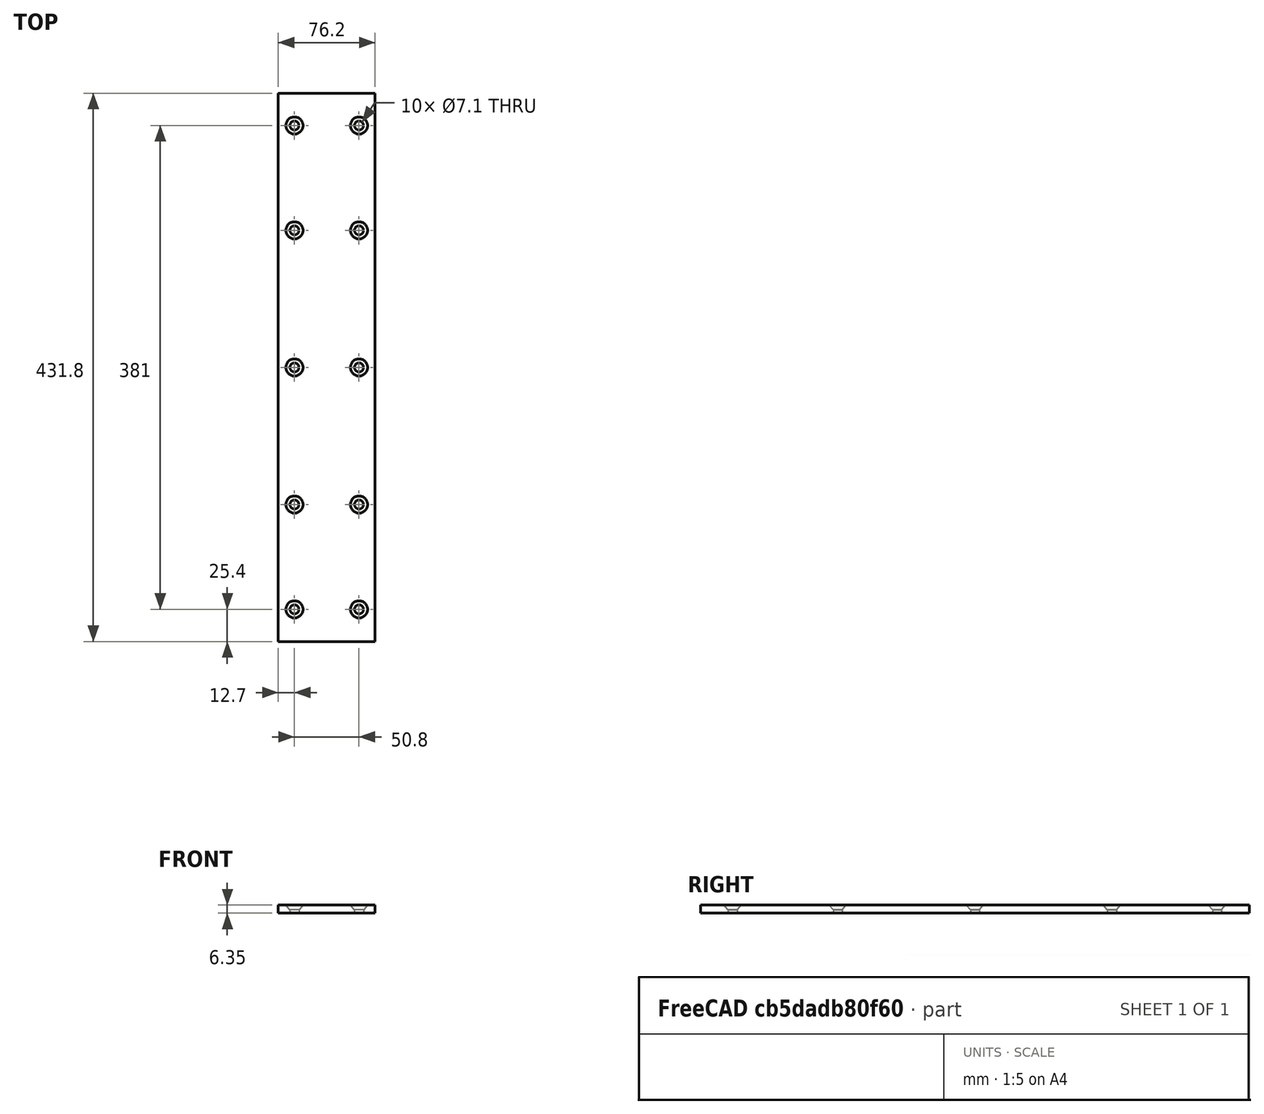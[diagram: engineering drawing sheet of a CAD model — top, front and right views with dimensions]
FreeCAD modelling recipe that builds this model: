
FCSTD DOCUMENT  (FreeCAD 0.20R29603 (Git))
Label: zero_clearance_insert
License: All rights reserved
LicenseURL: http://en.wikipedia.org/wiki/All_rights_reserved
objects: TechDraw::DrawViewDimension×8, TechDraw::DrawProjGroupItem×3, Sketcher::SketchObject×2, PartDesign::Pad×1, PartDesign::Hole×1, PartDesign::Body×1, TechDraw::DrawSVGTemplate×1, TechDraw::DrawProjGroup×1, TechDraw::DrawPage×1
note: 7 computed .brp shape members not serialized (recipe doc carries the construction recipe); baked Part::Feature solids carry a one-line shape summary decoded from their .brp

FEATURE [Sketcher::SketchObject] Sketch
  FullyConstrained = true
  MapMode = 5
  Support = -> [XY_Plane]
  sketch-geometry (5):
    g0: LineSegment StartX=-38.1 StartY=-215.9 StartZ=0 EndX=-38.1 EndY=215.9 EndZ=0
    g1: LineSegment StartX=-38.1 StartY=215.9 StartZ=0 EndX=38.1 EndY=215.9 EndZ=0
    g2: LineSegment StartX=38.1 StartY=215.9 StartZ=0 EndX=38.1 EndY=-215.9 EndZ=0
    g3: LineSegment StartX=38.1 StartY=-215.9 StartZ=0 EndX=-38.1 EndY=-215.9 EndZ=0
    g4: GeomPoint X=0 Y=0 Z=0
  constraints (12):
    c: Coincident(g0,g1)
    c: Coincident(g1,g2)
    c: Coincident(g2,g3)
    c: Coincident(g3,g0)
    c: Horizontal(g1)
    c: Horizontal(g3)
    c: Vertical(g0)
    c: Vertical(g2)
    c: Symmetric(g1,g0,g4)
    c: DistanceX(g1,g1) = 76.2
    c: DistanceY(g2,g2) = 431.8
    c: Coincident(g4,g-1)
FEATURE [PartDesign::Pad] Pad
  Direction = (0,0,1)
  Length = 6.35
  Length2 = 10
  Profile = -> Sketch
  ReferenceAxis = -> Sketch [N_Axis]
  Type = 0
FEATURE [Sketcher::SketchObject] Sketch001
  ExternalGeometry = -> [Pad]
  FullyConstrained = true
  MapMode = 5
  Placement = pos=(0,0,6.35) rot=(0,0,1;0rad)
  Support = -> [Pad]
  sketch-geometry (14):
    g0: LineSegment StartX=-25.4 StartY=215.9 StartZ=0 EndX=-25.4 EndY=-215.9 EndZ=0
    g1: LineSegment StartX=25.4 StartY=-215.9 StartZ=0 EndX=25.4 EndY=215.9 EndZ=0
    g2: Circle CenterX=-25.4 CenterY=190.5 CenterZ=0 NormalX=0 NormalY=0 NormalZ=1 AngleXU=0 Radius=3.175
    g3: Circle CenterX=-25.4 CenterY=0 CenterZ=0 NormalX=0 NormalY=0 NormalZ=1 AngleXU=0 Radius=3.175
    g4: Circle CenterX=-25.4 CenterY=107.95 CenterZ=0 NormalX=0 NormalY=0 NormalZ=1 AngleXU=0 Radius=3.175
    g5: LineSegment StartX=-25.4 StartY=215.9 StartZ=0 EndX=-25.4 EndY=107.95 EndZ=0
    g6: LineSegment StartX=-25.4 StartY=107.95 StartZ=0 EndX=-25.4 EndY=0 EndZ=0
    g7: Circle CenterX=-25.4 CenterY=-190.5 CenterZ=0 NormalX=0 NormalY=0 NormalZ=1 AngleXU=0 Radius=3.175
    g8: Circle CenterX=-25.4 CenterY=-107.95 CenterZ=0 NormalX=0 NormalY=0 NormalZ=1 AngleXU=0 Radius=3.175
    g9: Circle CenterX=25.4 CenterY=-190.5 CenterZ=0 NormalX=0 NormalY=0 NormalZ=1 AngleXU=0 Radius=3.175
    g10: Circle CenterX=25.4 CenterY=-107.95 CenterZ=0 NormalX=0 NormalY=0 NormalZ=1 AngleXU=0 Radius=3.175
    g11: Circle CenterX=25.4 CenterY=0 CenterZ=0 NormalX=0 NormalY=0 NormalZ=1 AngleXU=0 Radius=3.175
    g12: Circle CenterX=25.4 CenterY=107.95 CenterZ=0 NormalX=0 NormalY=0 NormalZ=1 AngleXU=0 Radius=3.175
    g13: Circle CenterX=25.4 CenterY=190.5 CenterZ=0 NormalX=0 NormalY=0 NormalZ=1 AngleXU=0 Radius=3.175
  constraints (43):
    c: Vertical(g0)
    c: Vertical(g1)
    c: PointOnObject(g1,g-3)
    c: PointOnObject(g0,g-3)
    c: PointOnObject(g0,g-6)
    c: PointOnObject(g1,g-6)
    c: Distance(g0,g-6) = 12.7
    c: Distance(g1,g-6) = 12.7
    c: Diameter(g2) = 6.35
    c: PointOnObject(g2,g0)
    c: Distance(g2,g-3) = 25.4
    c: PointOnObject(g3,g-1)
    c: PointOnObject(g3,g0)
    c: Equal(g2,g3)
    c: Equal(g3,g4)
    c: PointOnObject(g4,g0)
    c: Coincident(g5,g4)
    c: PointOnObject(g5,g-3)
    c: Vertical(g5)
    c: Coincident(g6,g3)
    c: Coincident(g6,g4)
    c: Equal(g5,g6)
    c: Distance(g7,g-6) = 25.4
    c: PointOnObject(g7,g0)
    c: Distance(g8,g-6) = 107.95
    c: PointOnObject(g8,g0)
    c: Equal(g8,g7)
    c: Equal(g7,g2)
    c: Diameter(g13) = 6.35
    c: Equal(g13,g11)
    c: Equal(g11,g12)
    c: Equal(g10,g9)
    c: Equal(g9,g13)
    c: Distance(g9,g-6) = 25.4
    c: PointOnObject(g9,g1)
    c: PointOnObject(g10,g1)
    c: PointOnObject(g11,g1)
    c: PointOnObject(g11,g-1)
    c: PointOnObject(g12,g1)
    c: Distance(g13,g-3) = 25.4
    c: PointOnObject(g13,g1)
    c: Distance(g12,g-3) = 107.95
    c: Distance(g10,g-6) = 107.95
FEATURE [PartDesign::Hole] Hole
  BaseFeature = -> Pad
  CustomThreadClearance = 0
  Depth = 885.806
  DepthType = 1
  Diameter = 7.1
  DrillForDepth = false
  DrillPoint = 1
  DrillPointAngle = 118
  HoleCutCountersinkAngle = 81
  HoleCutCustomValues = false
  HoleCutDepth = 0
  HoleCutDiameter = 13.4938
  HoleCutType = 2
  ModelThread = false
  Profile = -> Sketch001
  Tapered = false
  TaperedAngle = 90
  ThreadClass = 0
  ThreadDepth = 885.806
  ThreadDepthType = 0
  ThreadDirection = 0
  ThreadFit = 0
  ThreadSize = 9
  ThreadType = 3
  Threaded = false
  UseCustomThreadClearance = false
FEATURE [PartDesign::Body] Body
  Group = -> [Sketch,Pad,Sketch001,Hole]
  Origin = -> Origin
  Tip = -> Hole
FEATURE [TechDraw::DrawSVGTemplate] Template
  Height = 297
  Orientation = 1
  Width = 420
FEATURE [TechDraw::DrawProjGroupItem] ProjItem  label="Front"
  CoarseView = false
  Direction = (0,0,1)
  Focus = 100
  HardHidden = false
  IsoCount = 0
  IsoHidden = false
  IsoVisible = false
  LockPosition = true
  Perspective = false
  Rotation = 0
  RotationVector = (1,0,0)
  Scale = 0.5
  ScaleType = 2
  SeamHidden = false
  SeamVisible = true
  SmoothHidden = false
  SmoothVisible = true
  Source = -> [Body]
  Type = 0
  X = 0
  XDirection = (1e-16,-1,0)
  Y = 0
FEATURE [TechDraw::DrawProjGroupItem] ProjItem001  label="Left"
  CoarseView = false
  Direction = (-1e-16,1,1e-16)
  Focus = 100
  HardHidden = false
  IsoCount = 0
  IsoHidden = false
  IsoVisible = false
  LockPosition = false
  Perspective = false
  Rotation = 0
  RotationVector = (1,0,0)
  Scale = 0.5
  ScaleType = 2
  SeamHidden = false
  SeamVisible = true
  SmoothHidden = false
  SmoothVisible = true
  Source = -> [Body]
  Type = 1
  X = 230.981
  XDirection = (0,-1e-16,1)
  Y = 0
FEATURE [TechDraw::DrawProjGroupItem] ProjItem002  label="FrontTopRight"
  CoarseView = false
  Direction = (0.57735,-0.57735,0.57735)
  Focus = 100
  HardHidden = false
  IsoCount = 0
  IsoHidden = false
  IsoVisible = false
  LockPosition = false
  Perspective = false
  Rotation = 0
  RotationVector = (1,0,0)
  Scale = 0.5
  ScaleType = 2
  SeamHidden = false
  SeamVisible = true
  SmoothHidden = false
  SmoothVisible = true
  Source = -> [Body]
  Type = 7
  X = 147.001
  XDirection = (0,-0.707107,-0.707107)
  Y = 86.9946
FEATURE [TechDraw::DrawProjGroup] ProjGroup
  Anchor = -> ProjItem
  AutoDistribute = true
  LockPosition = false
  ProjectionType = 0
  Rotation = 0
  Scale = 0.5
  ScaleType = 0
  Source = -> [Body]
  Views = -> [ProjItem,ProjItem001,ProjItem002]
  X = 169.962
  Y = 139.782
  spacingX = 15.0812
  spacingY = 15.0812
FEATURE [TechDraw::DrawViewDimension] Dimension
  AngleOverride = false
  Arbitrary = false
  ArbitraryTolerances = false
  EqualTolerance = true
  ExtensionAngle = 0
  FormatSpec = ⌀%.2w 10x
  FormatSpecOverTolerance = %+.2w
  FormatSpecUnderTolerance = %+.2w
  Inverted = false
  LineAngle = 0
  LockPosition = false
  MeasureType = 1
  OverTolerance = 0
  References2D = -> [ProjItem]
  Rotation = 0
  Scale = 0.5
  ScaleType = 0
  TheoreticalExact = false
  Type = 5
  UnderTolerance = 0
  X = 75.0786
  Y = 40.8996
FEATURE [TechDraw::DrawViewDimension] Dimension001
  AngleOverride = false
  Arbitrary = false
  ArbitraryTolerances = false
  EqualTolerance = true
  ExtensionAngle = 0
  FormatSpec = %.2w
  FormatSpecOverTolerance = %+.2w
  FormatSpecUnderTolerance = %+.2w
  Inverted = false
  LineAngle = 0
  LockPosition = false
  MeasureType = 1
  OverTolerance = 0
  References2D = -> [ProjItem]
  Rotation = 0
  Scale = 0.5
  ScaleType = 0
  TheoreticalExact = false
  Type = 1
  UnderTolerance = 0
  X = -81.4561
  Y = -33.3394
FEATURE [TechDraw::DrawViewDimension] Dimension002
  AngleOverride = false
  Arbitrary = false
  ArbitraryTolerances = false
  EqualTolerance = true
  ExtensionAngle = 0
  FormatSpec = %.2w
  FormatSpecOverTolerance = %+.2w
  FormatSpecUnderTolerance = %+.2w
  Inverted = false
  LineAngle = 0
  LockPosition = false
  MeasureType = 1
  OverTolerance = 0
  References2D = -> [ProjItem]
  Rotation = 0
  Scale = 0.5
  ScaleType = 0
  TheoreticalExact = false
  Type = 0
  UnderTolerance = 0
  X = -73.7758
  Y = -39.1239
FEATURE [TechDraw::DrawViewDimension] Dimension003
  AngleOverride = false
  Arbitrary = false
  ArbitraryTolerances = false
  EqualTolerance = true
  ExtensionAngle = 0
  FormatSpec = %.2w
  FormatSpecOverTolerance = %+.2w
  FormatSpecUnderTolerance = %+.2w
  Inverted = false
  LineAngle = 0
  LockPosition = false
  MeasureType = 1
  OverTolerance = 0
  References2D = -> [ProjItem]
  Rotation = 0
  Scale = 0.5
  ScaleType = 0
  TheoreticalExact = false
  Type = 0
  UnderTolerance = 0
  X = -59.1242
  Y = -47.5391
FEATURE [TechDraw::DrawViewDimension] Dimension004
  AngleOverride = false
  Arbitrary = false
  ArbitraryTolerances = false
  EqualTolerance = true
  ExtensionAngle = 0
  FormatSpec = %.2w
  FormatSpecOverTolerance = %+.2w
  FormatSpecUnderTolerance = %+.2w
  Inverted = false
  LineAngle = 0
  LockPosition = false
  MeasureType = 1
  OverTolerance = 0
  References2D = -> [ProjItem]
  Rotation = 0
  Scale = 0.5
  ScaleType = 0
  TheoreticalExact = false
  Type = 1
  UnderTolerance = 0
  X = 3.51934
  Y = -54.9531
FEATURE [TechDraw::DrawViewDimension] Dimension005
  AngleOverride = false
  Arbitrary = false
  ArbitraryTolerances = false
  EqualTolerance = true
  ExtensionAngle = 0
  FormatSpec = %.2w
  FormatSpecOverTolerance = %+.2w
  FormatSpecUnderTolerance = %+.2w
  Inverted = false
  LineAngle = 0
  LockPosition = false
  MeasureType = 1
  OverTolerance = 0
  References2D = -> [ProjItem]
  Rotation = 0
  Scale = 0.5
  ScaleType = 0
  TheoreticalExact = false
  Type = 2
  UnderTolerance = 0
  X = -130.198
  Y = -0.037326
FEATURE [TechDraw::DrawViewDimension] Dimension006
  AngleOverride = false
  Arbitrary = false
  ArbitraryTolerances = false
  EqualTolerance = true
  ExtensionAngle = 0
  FormatSpec = %.2w
  FormatSpecOverTolerance = %+.2w
  FormatSpecUnderTolerance = %+.2w
  Inverted = false
  LineAngle = 0
  LockPosition = false
  MeasureType = 1
  OverTolerance = 0
  References2D = -> [ProjItem001]
  Rotation = 0
  Scale = 0.5
  ScaleType = 0
  TheoreticalExact = false
  Type = 1
  UnderTolerance = 0
  X = -13.3031
  Y = 20.6343
FEATURE [TechDraw::DrawViewDimension] Dimension007
  AngleOverride = false
  Arbitrary = false
  ArbitraryTolerances = false
  EqualTolerance = true
  ExtensionAngle = 0
  FormatSpec = %.2w
  FormatSpecOverTolerance = %+.2w
  FormatSpecUnderTolerance = %+.2w
  Inverted = false
  LineAngle = 0
  LockPosition = false
  MeasureType = 1
  OverTolerance = 0
  References2D = -> [ProjItem]
  Rotation = 0
  Scale = 0.5
  ScaleType = 0
  TheoreticalExact = false
  Type = 2
  UnderTolerance = 0
  X = -119.661
  Y = -26.9677
FEATURE [TechDraw::DrawPage] Page
  KeepUpdated = true
  NextBalloonIndex = 1
  ProjectionType = 0
  Scale = 0.5
  Template = -> Template
  Views = -> [ProjGroup,Dimension,Dimension001,Dimension002,Dimension003,Dimension004,Dimension005,Dimension006,Dimension007]
